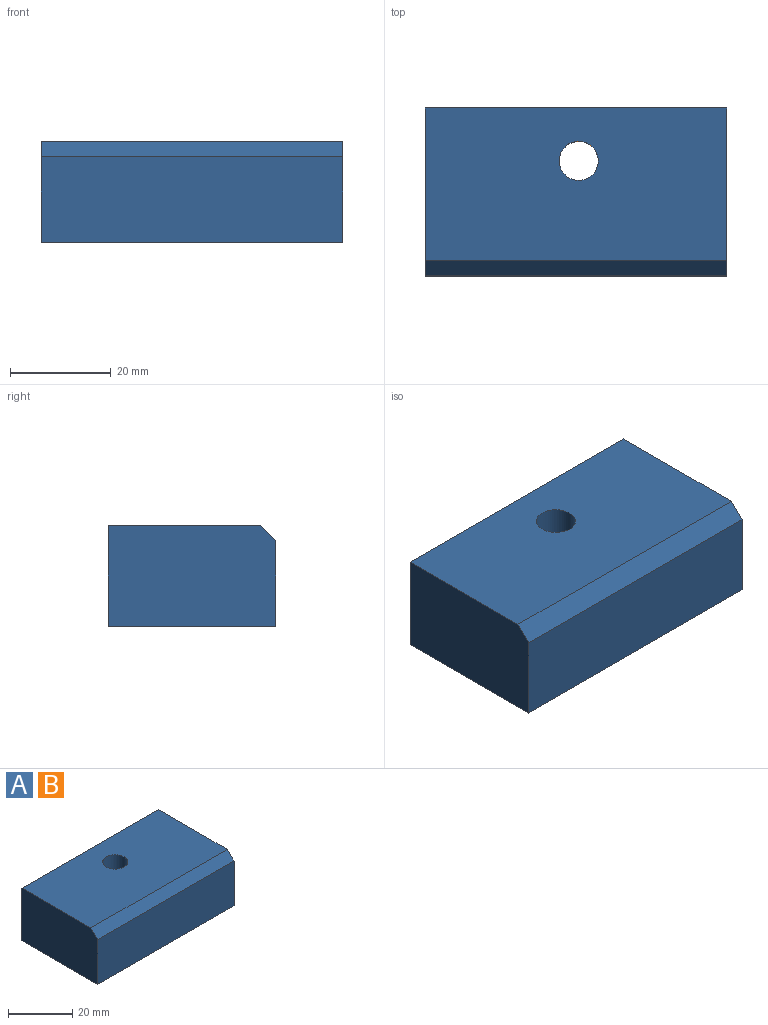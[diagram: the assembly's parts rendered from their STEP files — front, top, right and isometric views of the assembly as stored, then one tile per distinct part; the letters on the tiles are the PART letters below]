
ASSEMBLY  parts=2 mates=1
PART A: 8 faces, bbox 59.8x33.2x20 mm
  f0: plane 33.25x20mm, normal (1,0,0), area 660.5mm2, adj f1,f3,f4,f5,f6
  f1: plane 59.77x20mm, normal (0,1,0), area 1195.3mm2, adj f0,f2,f4,f5
  f2: plane 33.25x20mm, normal (-1,0,0), area 660.5mm2, adj f1,f3,f4,f5,f6
  f3: plane 59.77x17mm, normal (0,-1,0), area 1016mm2, adj f0,f2,f5,f6
  f4: plane 59.77x30.25mm, normal (0,0,1), area 1760.8mm2, adj f0,f1,f2,f6,f7
  f5: plane 59.77x33.25mm, normal (0,0,-1), area 1940.1mm2, adj f0,f1,f2,f3,f7
  f6: plane 59.77x3mm, normal (0,-0.71,0.71), area 253.6mm2, adj f0,f2,f3,f4
  f7: cylinder r=3.87mm len=20mm, axis (0,0,1), area 486.5mm2, adj f4,f5
PART B: same geometry as A
PLACE A at identity
PLACE B at identity fixed
MATE fastened A.f4 <-> B.f4  axis (0,0,1) through (-29.9,-15.25,20)mm
